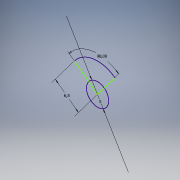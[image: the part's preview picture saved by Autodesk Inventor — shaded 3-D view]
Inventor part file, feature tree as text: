
AUTODESK INVENTOR PART (.ipt)
format: ipt  version: 2019.4 (Build 234330000, 330)  size: 99,840 bytes
history: native  units: mm
features: extrude x1, sketch x1
ambient origin geometry x8: Origin, YZ Plane, XZ Plane, XY Plane, X Axis, Y Axis, Z Axis, Center Point
bodies: Solid1 (feature_tree)
feature tree (2):
  extrude  "Extrusion1"  Depth=6.5mm
  sketch  "Sketch1"  dims[d0=5.0mm d2=6.5mm d4=3.5mm d5=0.0mm]
